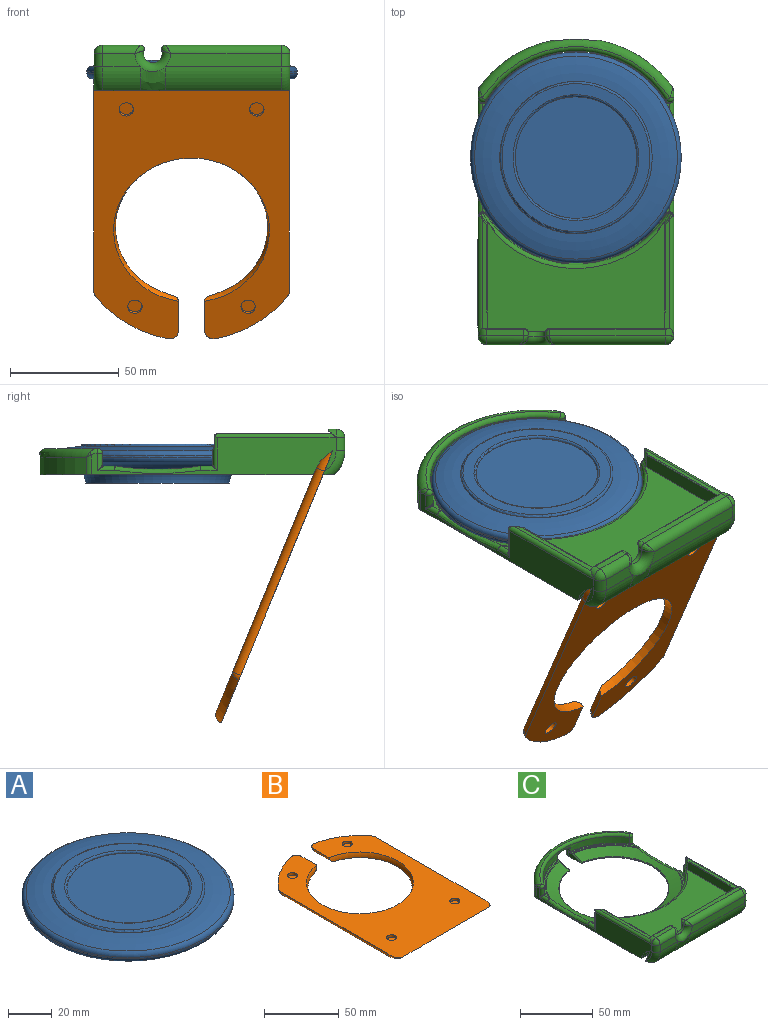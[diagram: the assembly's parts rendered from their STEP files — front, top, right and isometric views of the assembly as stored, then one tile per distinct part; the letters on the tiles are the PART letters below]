
ASSEMBLY  parts=3 mates=2
PART A: 13 faces, bbox 104.8x104.8x18.6 mm
  f0: torus R=34mm, axis (0,0,1), area 3039.4mm2, adj f1,f10
  f1: cylinder r=35mm len=70mm, axis (0,0,1), area 27.8mm2, adj f0,f11
  f2: plane 68x68mm, normal (0,0,1), area 1003.9mm2, adj f11,f12
  f3: cylinder r=27.92mm len=55.84mm, axis (0,0,1), area 22.2mm2, adj f4,f12
  f4: plane 55.84x55.84mm, normal (0,0,1), area 2449.2mm2, adj f3
  f5: plane 66x66mm, normal (0,0,-1), area 3421.2mm2, adj f8
  f6: plane 91.8x91.8mm, normal (0,0,-1), area 813.3mm2, adj f8,f9
  f7: cylinder r=48.4mm len=96.8mm, axis (0,0,1), area 213.6mm2, adj f9,f10
  f8: torus R=42.99mm, axis (0,0,1), area 3510.7mm2, adj f5,f6
  f9: torus R=45.9mm, axis (0,0,1), area 1171.8mm2, adj f6,f7
  f10: torus R=45.9mm, axis (0,0,-1), area 952.4mm2, adj f0,f7
  f11: torus R=34mm, axis (0,0,-1), area 341.8mm2, adj f1,f2
  f12: torus R=28.92mm, axis (0,0,-1), area 279.2mm2, adj f2,f3
PART B: 26 faces, bbox 100.4x149.3x27.1 mm
  f0: plane 140.23x94.66mm, normal (0,0,1), area 7205.1mm2, adj f1,f2,f3,f4,f5,f6,f8,f9
  f1: torus R=45mm, axis (0,0,1), area 845.8mm2, adj f0,f7,f8,f16
  f2: torus R=11mm, axis (-1,0,0), area 33.4mm2, adj f0,f3,f10
  f3: cylinder r=15mm len=58.41mm, axis (1,0,0), area 655mm2, adj f0,f2,f4,f7
  f4: bspline ~15.36x15.32mm, area 134.1mm2, adj f0,f3,f5,f7
  f5: cylinder r=15mm len=10.41mm, axis (1,0,0), area 116.7mm2, adj f0,f4,f6,f7
  f6: torus R=11mm, axis (-1,0,0), area 33.4mm2, adj f0,f5,f11
  f7: plane 121.38x82mm, normal (0,0,-1), area 5322.2mm2, adj f1,f3,f4,f5,f8,f9,f10,f11
  f8: cylinder r=4mm len=16.47mm, axis (0,-1,0), area 97.9mm2, adj f0,f1,f7,f12
  f9: torus R=51mm, axis (0,0,1), area 247.8mm2, adj f0,f7,f12,f13
  f10: cylinder r=4mm len=101.29mm, axis (0,1,0), area 636.4mm2, adj f0,f2,f7,f13
  f11: cylinder r=4mm len=101.29mm, axis (0,-1,0), area 636.4mm2, adj f0,f6,f7,f14
  f12: sphere r=4mm, area 19.2mm2, adj f0,f8,f9
  f13: sphere r=4mm, area 6.5mm2, adj f0,f9,f10
  f14: sphere r=4mm, area 10.2mm2, adj f0,f11,f15
  f15: torus R=51mm, axis (0,0,1), area 247.8mm2, adj f0,f7,f14,f17
  f16: cylinder r=4mm len=16.47mm, axis (0,1,0), area 97.9mm2, adj f0,f1,f7,f17
  f17: sphere r=4mm, area 18mm2, adj f0,f15,f16
  f18: cylinder r=3.3mm len=6.6mm, axis (0,0,1), area 41.5mm2, adj f0,f19
  f19: plane 6.6x6.6mm, normal (0,0,1), area 34.3mm2, adj f18
  f20: cylinder r=3.3mm len=6.6mm, axis (0,0,1), area 41.5mm2, adj f0,f21
  f21: plane 6.6x6.6mm, normal (0,0,1), area 34.3mm2, adj f20
  f22: cylinder r=3.3mm len=6.6mm, axis (0,0,1), area 41.5mm2, adj f0,f23
  f23: plane 6.6x6.6mm, normal (0,0,1), area 34.3mm2, adj f22
  f24: cylinder r=3.3mm len=6.6mm, axis (0,0,1), area 41.5mm2, adj f0,f25
  f25: plane 6.6x6.6mm, normal (0,0,1), area 34.3mm2, adj f24
PART C: 151 faces, bbox 102.5x151x26.9 mm
  f0: cylinder r=51mm len=5.04mm, axis (0,0,-1), area 28.7mm2, adj f4,f8,f139,f140,f141,f150
  f1: plane 51.66x2.5mm, normal (0,0,1), area 104.3mm2, adj f2,f25,f90,f91,f141,f150
  f2: cylinder r=2mm len=38.84mm, axis (0,-1,0), area 19.5mm2, adj f1,f8,f91,f150
  f3: bspline ~4.75x2.52mm, area 0.6mm2, adj f7,f27,f30
  f4: torus R=49mm, axis (0,0,-1), area 13mm2, adj f0,f9,f27,f30,f138,f148,f150
  f5: bspline ~4.16x2.37mm, area 0.6mm2, adj f9,f27,f30
  f6: torus R=12mm, axis (0,0,1), area 0.9mm2, adj f36,f56,f149
  f7: bspline ~0.81x0.63mm, area 0mm2, adj f3,f27,f88
  f8: bspline ~1.57x1.49mm, area 0.3mm2, adj f0,f2,f141,f150
  f9: bspline ~0.81x0.63mm, area 0mm2, adj f4,f5,f27
  f10: plane 36.5x28.3mm, normal (0,0,1), area 57.1mm2, adj f92,f104,f118,f122,f123
  f11: plane 86x28.74mm, normal (0,0,1), area 129.5mm2, adj f93,f99,f100,f143,f144,f145
  f12: plane 112.33x17mm, normal (-1,0,0), area 966.9mm2, adj f13,f17,f31,f34,f71,f72,f73,f86
  f13: plane 125.47x90mm, normal (0,0,-1), area 5846.3mm2, adj f12,f15,f16,f17,f22,f24,f43,f44
  f14: plane 91.84x7.51mm, normal (0,0,-1), area 457.9mm2, adj f18,f19,f20,f71,f83,f87
  f15: plane 112.33x17mm, normal (1,0,0), area 966.9mm2, adj f13,f16,f29,f32,f71,f72,f73,f82
  f16: cylinder r=4mm len=9.17mm, axis (0,0,1), area 21.9mm2, adj f13,f15,f24,f108
  f17: cylinder r=4mm len=9.17mm, axis (0,0,1), area 21.9mm2, adj f12,f13,f22,f105
  f18: cylinder r=15mm len=17.34mm, axis (1,0,0), area 214.1mm2, adj f14,f19,f21,f87
  f19: bspline ~11.7x11.33mm, area 130.3mm2, adj f14,f18,f20,f50
  f20: cylinder r=15mm len=53.34mm, axis (1,0,0), area 658.6mm2, adj f14,f19,f40,f83
  f21: plane 17.34x6mm, normal (0,-1,0), area 93.3mm2, adj f18,f50,f51,f86
  f22: cylinder r=55mm len=33.43mm, axis (0,0,1), area 324.1mm2, adj f13,f17,f47,f48
  f23: cylinder r=49mm len=82.63mm, axis (0,0,-1), area 491.3mm2, adj f32,f33,f34,f121,f122,f126,f127,f128
  f24: cylinder r=55mm len=33.43mm, axis (0,0,1), area 324.1mm2, adj f13,f16,f45,f47
  f25: plane 22.89x3.86mm, normal (0,0.64,-0.76), area 37.5mm2, adj f1,f37,f76,f77,f84,f85,f90
  f26: plane 17.08x3mm, normal (0,0,1), area 51.3mm2, adj f51,f54,f76,f84
  f27: plane 81.07x50.07mm, normal (0,0,1), area 2843.9mm2, adj f3,f4,f5,f7,f9,f30,f37,f88
  f28: cylinder r=49mm len=82.63mm, axis (0,0,-1), area 540.7mm2, adj f29,f30,f31,f144
  f29: cylinder r=2mm len=16.18mm, axis (0,0,-1), area 46.2mm2, adj f15,f28,f89,f131,f132,f133,f134,f142
  f30: torus R=51mm, axis (0,0,1), area 298.2mm2, adj f3,f4,f5,f27,f28,f88,f131,f137
  f31: cylinder r=2mm len=16.18mm, axis (0,0,-1), area 46.2mm2, adj f12,f28,f90,f137,f138,f139,f140,f145
  f32: cylinder r=2mm len=8mm, axis (0,0,-1), area 32.2mm2, adj f15,f23,f110,f114,f118
  f33: torus R=51mm, axis (0,0,1), area 313.4mm2, adj f23,f47,f107,f110
  f34: cylinder r=2mm len=8mm, axis (0,0,-1), area 32.2mm2, adj f12,f23,f107,f113,f117
  f35: cylinder r=51mm len=5.04mm, axis (0,0,-1), area 28.7mm2, adj f88,f133,f134,f135,f136,f149
  f36: plane 51.66x2.5mm, normal (0,0,1), area 104.3mm2, adj f6,f38,f56,f89,f135,f149
  f37: plane 81x7.87mm, normal (0,1,0), area 522.4mm2, adj f25,f27,f38,f41,f52,f54,f77,f79
  f38: plane 58.89x3.86mm, normal (0,0.64,-0.76), area 100mm2, adj f36,f37,f78,f79,f80,f81,f89
  f39: plane 53.08x3mm, normal (0,0,1), area 159.4mm2, adj f49,f52,f78,f80
  f40: plane 53.34x6mm, normal (0,-1,0), area 309.3mm2, adj f20,f49,f50,f82
  f41: cylinder r=4.25mm len=8.5mm, axis (0,-1,0), area 32.2mm2, adj f37,f50,f52,f54
  f42: plane 10.11x1.75mm, normal (0,0,-1), area 15.1mm2, adj f46,f57,f58,f60,f61,f130
  f43: plane 12.91x7.02mm, normal (1,0,0), area 33.7mm2, adj f13,f48,f60,f111,f112,f116,f120,f124
  f44: plane 12.91x7.02mm, normal (-1,0,0), area 33.7mm2, adj f13,f45,f57,f111,f115,f119,f123,f125
  f45: cylinder r=4mm len=9.79mm, axis (0,0,1), area 57.6mm2, adj f13,f24,f44,f47,f58,f59
  f46: torus R=51mm, axis (0,0,-1), area 55.4mm2, adj f42,f47,f59,f62
  f47: torus R=51mm, axis (0,0,1), area 608.9mm2, adj f22,f24,f33,f45,f46,f48,f59,f62
  f48: cylinder r=4mm len=9.79mm, axis (0,0,1), area 57.6mm2, adj f13,f22,f43,f47,f61,f62
  f49: cylinder r=4mm len=53.08mm, axis (-1,0,0), area 326.2mm2, adj f39,f40,f53,f81
  f50: torus R=8.25mm, axis (0,-1,0), area 122.8mm2, adj f19,f21,f40,f41,f53,f55
  f51: cylinder r=4mm len=17.08mm, axis (-1,0,0), area 100mm2, adj f21,f26,f55,f85
  f52: cylinder r=2mm len=3mm, axis (0,-1,0), area 8.7mm2, adj f37,f39,f41,f53,f79
  f53: bspline ~5.12x4.88mm, area 11.3mm2, adj f49,f50,f52
  f54: cylinder r=2mm len=3mm, axis (0,-1,0), area 8.7mm2, adj f26,f37,f41,f55,f77
  f55: bspline ~5.12x4.88mm, area 11.3mm2, adj f50,f51,f54
  f56: cylinder r=2mm len=38.84mm, axis (0,1,0), area 19.5mm2, adj f6,f36,f136,f149
  f57: cylinder r=1mm len=1mm, axis (0,-1,0), area 1.3mm2, adj f42,f44,f58,f129
  f58: torus R=5mm, axis (0,0,-1), area 1mm2, adj f42,f45,f57,f59
  f59: bspline ~4.06x4.01mm, area 6.1mm2, adj f45,f46,f47,f58
  f60: cylinder r=1mm len=1mm, axis (0,1,0), area 1.3mm2, adj f42,f43,f61,f128
  f61: torus R=5mm, axis (0,0,-1), area 1mm2, adj f42,f48,f60,f62
  f62: bspline ~4.06x4.01mm, area 6.1mm2, adj f46,f47,f48,f61
  f63: cylinder r=3.3mm len=6.6mm, axis (0,0,-1), area 41.5mm2, adj f13,f64
  f64: plane 6.6x6.6mm, normal (0,0,-1), area 34.3mm2, adj f63
  f65: cylinder r=3.3mm len=6.6mm, axis (0,0,-1), area 41.5mm2, adj f13,f66
  f66: plane 6.6x6.6mm, normal (0,0,-1), area 34.3mm2, adj f65
  f67: cylinder r=3.3mm len=6.6mm, axis (0,0,-1), area 41.5mm2, adj f13,f68
  f68: plane 6.6x6.6mm, normal (0,0,-1), area 34.3mm2, adj f67
  f69: cylinder r=3.3mm len=6.6mm, axis (0,0,-1), area 41.5mm2, adj f13,f70
  f70: plane 6.6x6.6mm, normal (0,0,-1), area 34.3mm2, adj f69
  f71: plane 90.08x11.08mm, normal (0,0.93,0.38), area 1069.9mm2, adj f12,f14,f15,f72,f83,f87
  f72: cylinder r=18.93mm len=90mm, axis (-1,0,0), area 1157mm2, adj f12,f15,f71,f73
  f73: plane 90x1.59mm, normal (0,-0.93,-0.38), area 155.1mm2, adj f12,f13,f15,f72
  f74: plane 36.5x28.3mm, normal (0,0,1), area 57.1mm2, adj f94,f95,f117,f120,f121
  f75: cone r=35mm half-angle=71.6deg, axis (0,0,1), area 2336.1mm2, adj f92,f93,f94,f97,f102,f111,f112,f115
  f76: cylinder r=0.5mm len=19.58mm, axis (-1,0,0), area 22.4mm2, adj f25,f26,f77,f84
  f77: bspline ~2.99x2.67mm, area 3.1mm2, adj f25,f37,f54,f76
  f78: cylinder r=0.5mm len=55.58mm, axis (-1,0,0), area 66.3mm2, adj f38,f39,f79,f80
  f79: bspline ~2.99x2.67mm, area 3.1mm2, adj f37,f38,f52,f78
  f80: cylinder r=4mm len=3.99mm, axis (0,-1,0), area 14mm2, adj f38,f39,f78,f81
  f81: sphere r=4mm, area 25.1mm2, adj f38,f49,f80,f82,f89
  f82: cylinder r=4mm len=6mm, axis (0,0,-1), area 37.7mm2, adj f15,f40,f81,f83
  f83: torus R=11mm, axis (-1,0,0), area 79.9mm2, adj f14,f15,f20,f71,f82
  f84: cylinder r=4mm len=3.99mm, axis (0,1,0), area 14mm2, adj f25,f26,f76,f85
  f85: sphere r=4mm, area 25.1mm2, adj f25,f51,f84,f86,f90
  f86: cylinder r=4mm len=6mm, axis (0,0,1), area 37.7mm2, adj f12,f21,f85,f87
  f87: torus R=11mm, axis (-1,0,0), area 79.9mm2, adj f12,f14,f18,f71,f86
  f88: torus R=49mm, axis (0,0,-1), area 13mm2, adj f7,f27,f30,f35,f132,f147,f149
  f89: cylinder r=2mm len=55.84mm, axis (0,-1,0), area 168.6mm2, adj f15,f29,f36,f38,f81,f134
  f90: cylinder r=2mm len=55.84mm, axis (0,1,0), area 168.6mm2, adj f1,f12,f25,f31,f85,f140
  f91: torus R=12mm, axis (0,0,1), area 0.9mm2, adj f1,f2,f150
  f92: torus R=47.32mm, axis (0,0,1), area 30.3mm2, adj f10,f75,f103,f119
  f93: torus R=47.32mm, axis (0,0,1), area 69mm2, adj f11,f75,f98,f101
  f94: torus R=47.32mm, axis (0,0,1), area 30.3mm2, adj f74,f75,f96,f116
  f95: cylinder r=2mm len=7.66mm, axis (0,1,0), area 20.1mm2, adj f12,f74,f96,f113
  f96: sphere r=2mm, area 0.6mm2, adj f94,f95,f97
  f97: bspline ~55.61x5.31mm, area 147.8mm2, adj f12,f75,f96,f98
  f98: sphere r=2mm, area 0.6mm2, adj f93,f97,f99
  f99: cylinder r=2mm len=7.66mm, axis (0,1,0), area 20.1mm2, adj f11,f12,f98,f146
  f100: cylinder r=2mm len=7.66mm, axis (0,-1,0), area 20.1mm2, adj f11,f15,f101,f142
  f101: sphere r=2mm, area 0.4mm2, adj f93,f100,f102
  f102: bspline ~55.61x5.31mm, area 147.8mm2, adj f15,f75,f101,f103
  f103: sphere r=2mm, area 0.6mm2, adj f92,f102,f104
  f104: cylinder r=2mm len=7.66mm, axis (0,-1,0), area 20.1mm2, adj f10,f15,f103,f114
  f105: bspline ~3.26x2.99mm, area 1.6mm2, adj f17,f47,f106
  f106: bspline ~5.12x3.37mm, area 9.1mm2, adj f12,f47,f105,f107
  f107: sphere r=2mm, area 12.6mm2, adj f33,f34,f106
  f108: bspline ~3.26x2.99mm, area 1.6mm2, adj f16,f47,f109
  f109: bspline ~5.12x3.37mm, area 9.1mm2, adj f15,f47,f108,f110
  f110: sphere r=2mm, area 8mm2, adj f32,f33,f109
  f111: torus R=38.08mm, axis (0,0,-1), area 317mm2, adj f13,f43,f44,f75,f112,f115
  f112: bspline ~28.96x9.98mm, area 7.3mm2, adj f43,f75,f111,f116
  f113: bspline ~2.5x2.5mm, area 1.1mm2, adj f34,f95,f117
  f114: bspline ~2.5x2.5mm, area 1.1mm2, adj f32,f104,f118
  f115: bspline ~28.96x9.98mm, area 7.3mm2, adj f44,f75,f111,f119
  f116: bspline ~1.5x0.72mm, area 0.5mm2, adj f43,f94,f112,f120
  f117: torus R=2.5mm, axis (0,0,1), area 1.7mm2, adj f34,f74,f113,f121
  f118: torus R=2.5mm, axis (0,0,1), area 1.7mm2, adj f10,f32,f114,f122
  f119: bspline ~1.2x0.61mm, area 0.5mm2, adj f44,f92,f115,f123
  f120: cylinder r=0.5mm len=1.19mm, axis (0,1,0), area 0.9mm2, adj f43,f74,f116,f124
  f121: torus R=48.5mm, axis (0,0,1), area 33.4mm2, adj f23,f74,f117,f124
  f122: torus R=48.5mm, axis (0,0,1), area 33.4mm2, adj f10,f23,f118,f125
  f123: cylinder r=0.5mm len=1.19mm, axis (0,-1,0), area 0.9mm2, adj f10,f44,f119,f125
  f124: bspline ~1.22x1.18mm, area 0.8mm2, adj f43,f120,f121,f126
  f125: bspline ~1.24x1.18mm, area 0.8mm2, adj f44,f122,f123,f127
  f126: cylinder r=0.5mm len=2.5mm, axis (0,0,-1), area 1.8mm2, adj f23,f43,f124,f128
  f127: cylinder r=0.5mm len=2.5mm, axis (0,0,-1), area 1.8mm2, adj f23,f44,f125,f129
  f128: bspline ~1.83x1.82mm, area 1.4mm2, adj f23,f60,f126,f130
  f129: bspline ~1.83x1.82mm, area 1.4mm2, adj f23,f57,f127,f130
  f130: torus R=49.5mm, axis (0,0,-1), area 7.8mm2, adj f23,f42,f128,f129
  f131: bspline ~2.08x1.87mm, area 0.6mm2, adj f29,f30,f132
  f132: bspline ~2.79x2mm, area 2mm2, adj f29,f88,f131,f133
  f133: cylinder r=0.5mm len=4.72mm, axis (0,0,1), area 4.4mm2, adj f29,f35,f132,f134
  f134: bspline ~4.05x2.7mm, area 2.6mm2, adj f29,f35,f89,f133,f135
  f135: torus R=51.5mm, axis (0,0,1), area 2.7mm2, adj f35,f36,f134,f136
  f136: bspline ~1.31x1.27mm, area 0.3mm2, adj f35,f56,f135,f149
  f137: bspline ~2.08x1.87mm, area 0.6mm2, adj f30,f31,f138
  f138: bspline ~2.79x2mm, area 2mm2, adj f4,f31,f137,f139
  f139: cylinder r=0.5mm len=4.72mm, axis (0,0,1), area 4.4mm2, adj f0,f31,f138,f140
  f140: bspline ~4.05x2.7mm, area 2.6mm2, adj f0,f31,f90,f139,f141
  f141: torus R=51.5mm, axis (0,0,1), area 2.7mm2, adj f0,f1,f8,f140
  f142: bspline ~2.5x2.5mm, area 1.1mm2, adj f29,f100,f143
  f143: torus R=2.5mm, axis (0,0,1), area 1.7mm2, adj f11,f29,f142,f144
  f144: torus R=48.5mm, axis (0,0,1), area 76.9mm2, adj f11,f28,f143,f145
  f145: torus R=2.5mm, axis (0,0,1), area 1.7mm2, adj f11,f31,f144,f146
  f146: bspline ~2.5x2.5mm, area 1.1mm2, adj f31,f99,f145
  f147: plane 0.05x0.04mm, normal (0,-1,0), area 0mm2, adj f27,f88,f149
  f148: plane 0.05x0.04mm, normal (0,-1,0), area 0mm2, adj f4,f27,f150
  f149: plane 50.26x7.26mm, normal (-1,0,0), area 340.9mm2, adj f6,f27,f35,f36,f37,f56,f88,f136
  f150: plane 50.26x7.26mm, normal (1,0,0), area 340.9mm2, adj f0,f1,f2,f4,f8,f27,f37,f91
PLACE A t=(0.09,15.54,-4.39)mm
PLACE B rot(axis=(0,0.83,-0.56),180deg) t=(-0.11,-30.47,-72.46)mm
PLACE C t=(0.09,15.54,-13.89)mm
MATE fastened B.f0 <-> C.f71  axis (0,-0.93,-0.38) through (-11.91,-64.98,1.11)mm
MATE fastened B.f0 <-> C.f71  axis (0,-0.93,-0.38) through (-11.91,-64.98,1.11)mm
